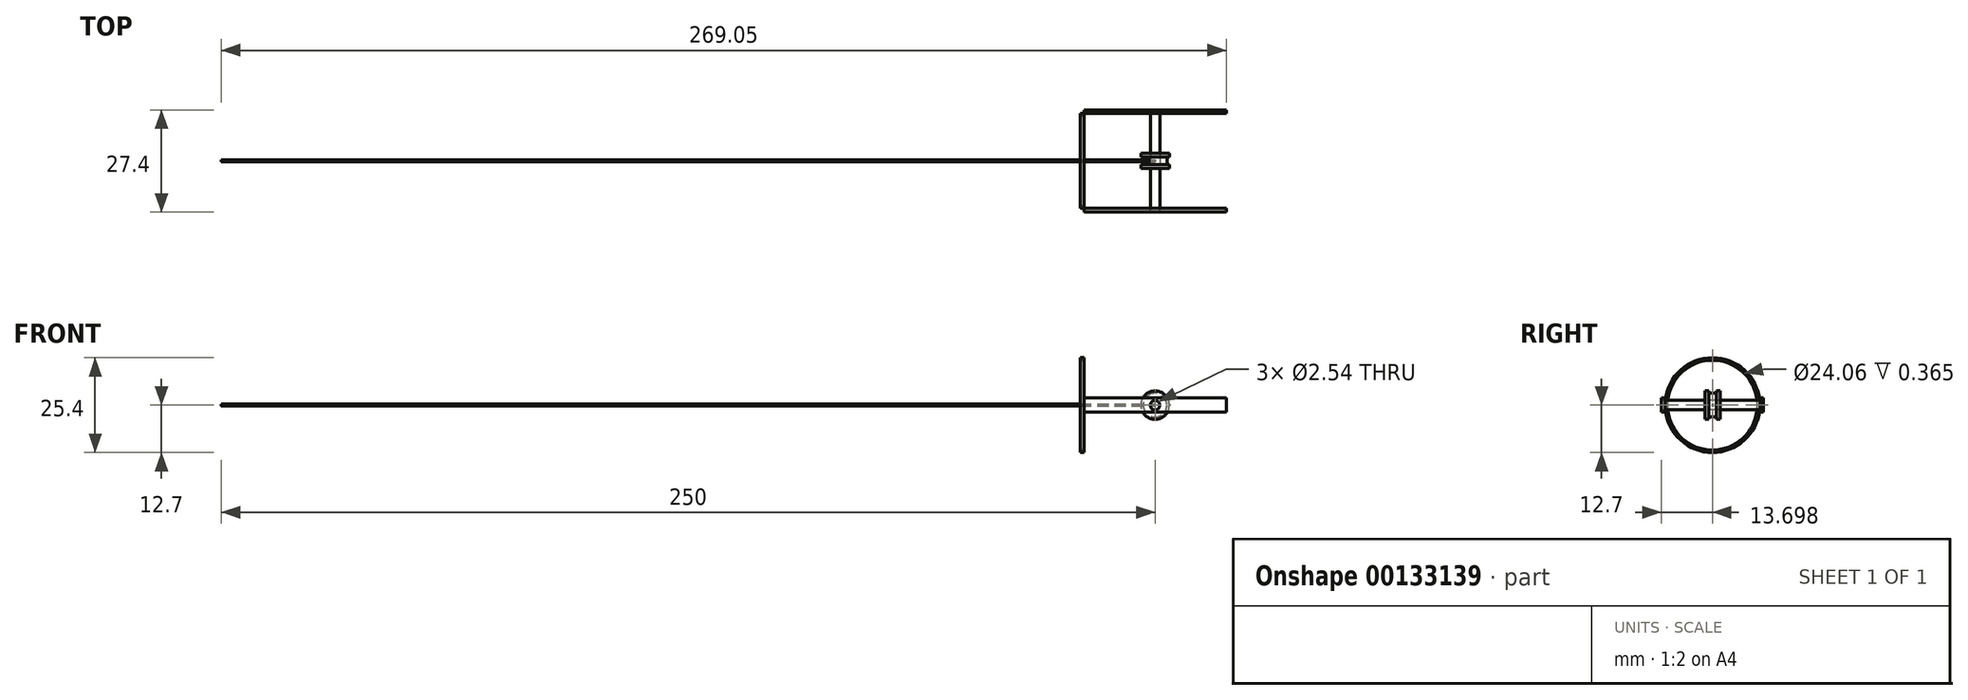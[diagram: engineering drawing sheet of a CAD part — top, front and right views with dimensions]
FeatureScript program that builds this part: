
annotation { "Feature Type Name" : "Feature", "Feature Type Description" : "" }
export const myFeature = defineFeature(function(context is Context, id is Id, definition is map)
    precondition{}
    {
        {
            var Q0;
            Q0=qCreatedBy(makeId("Front.planeOp"),FACE);
            var sketch = newSketch(context, id + "F0", { "sketchPlane" : qUnion([Q0])});
            skCircle(sketch, "E0", {"center": v(0, 0) * mm, "radius": 3.18 * mm});
            skCircle(sketch, "E1", {"center": v(0, 0) * mm, "radius": 3.81 * mm});
            skSolve(sketch);
        }
        {
            var Q0;
            Q0=makeQuery(id+"F0.imprint","IMPRINT",FACE,{"disambiguationData":[TD([[makeQuery(id+"F0.imprint","IMPRINT",EDGE,{"derivedFrom":sQuery(id+"F0.wireOp",EDGE,"E0")}),-1.0]])]});
            var Q1;
            Q1=makeQuery(id+"F0.imprint","IMPRINT",FACE,{"disambiguationData":[TD([[makeQuery(id+"F0.imprint","IMPRINT",EDGE,{"derivedFrom":sQuery(id+"F0.wireOp",EDGE,"E0")}),1.0]])]});
            extrude(context, id + "F1", {"entities" : qUnion([Q0, Q1]), "depth" : 1 * mm});
        }
        {
            var Q0;
            Q0=makeQuery(id+"F1.opExtrude","CAP_FACE",FACE,{"disambiguationData":[OSD([sQuery(id+"F0.wireOp",EDGE,"E1")])],"isStart":false});
            var sketch = newSketch(context, id + "F2", { "sketchPlane" : qUnion([Q0])});
            skCircle(sketch, "E2", {"center": v(0, 0) * mm, "radius": 3.18 * mm});
            skSolve(sketch);
        }
        {
            var Q0;
            Q0=makeQuery(id+"F2.imprint","IMPRINT",FACE,{"disambiguationData":[TD([[makeQuery(id+"F2.imprint","IMPRINT",EDGE,{"derivedFrom":sQuery(id+"F2.wireOp",EDGE,"E2")}),1.0]])]});
            extrude(context, id + "F3", {"entities" : qUnion([Q0]), "operationType" : NewBodyOperationType.ADD, "depth" : 2 * mm});
        }
        {
            var Q0;
            Q0=makeQuery(id+"F3.opExtrude","CAP_FACE",FACE,{"disambiguationData":[OSD([sQuery(id+"F2.wireOp",EDGE,"E2")])],"isStart":false});
            var sketch = newSketch(context, id + "F4", { "sketchPlane" : qUnion([Q0])});
            skCircle(sketch, "E3", {"center": v(0, 0) * mm, "radius": 3.81 * mm});
            skSolve(sketch);
        }
        {
            var Q0;
            Q0=makeQuery(id+"F4.imprint","IMPRINT",FACE,{"disambiguationData":[TD([[makeQuery(id+"F4.imprint","IMPRINT",EDGE,{"derivedFrom":sQuery(id+"F4.wireOp",EDGE,"E3")}),1.0]])]});
            var Q1;
            Q1=makeQuery(id+"F4.imprint","IMPRINT",FACE,{"disambiguationData":[TD([[makeQuery(id+"F4.imprint","IMPRINT",EDGE,{"derivedFrom":makeQuery(id+"F3.opExtrude","CAP_EDGE",EDGE,{"disambiguationData":[OSD([sQuery(id+"F2.wireOp",EDGE,"E2")])],"isStart":false})}),1.0]])]});
            extrude(context, id + "F5", {"entities" : qUnion([Q0, Q1]), "operationType" : NewBodyOperationType.ADD, "depth" : 1 * mm});
        }
        {
            var Q0;
            Q0=makeQuery(id+"F5.opExtrude","CAP_FACE",FACE,{"disambiguationData":[OSD([sQuery(id+"F4.wireOp",EDGE,"E3")])],"isStart":false});
            var sketch = newSketch(context, id + "F6", { "sketchPlane" : qUnion([Q0])});
            skCircle(sketch, "E4", {"center": v(0, 0) * mm, "radius": 1.27 * mm});
            skSolve(sketch);
        }
        {
            var Q0;
            Q0=makeQuery(id+"F6.imprint","IMPRINT",FACE,{"disambiguationData":[TD([[makeQuery(id+"F6.imprint","IMPRINT",EDGE,{"derivedFrom":sQuery(id+"F6.wireOp",EDGE,"E4")}),1.0]])]});
            extrude(context, id + "F7", {"entities" : qUnion([Q0]), "operationType" : NewBodyOperationType.REMOVE, "oppositeDirection" : true, "depth" : 25.4 * mm});
        }
        {
            var Q0;
            Q0=qCreatedBy(makeId("Front.planeOp"),FACE);
            var sketch = newSketch(context, id + "F8", { "sketchPlane" : qUnion([Q0])});
            skCircle(sketch, "E5", {"center": v(0, 0) * mm, "radius": 1.27 * mm});
            skSolve(sketch);
        }
        {
            var Q0;
            Q0=makeQuery(id+"F8.imprint","IMPRINT",FACE,{"disambiguationData":[TD([[makeQuery(id+"F8.imprint","IMPRINT",EDGE,{"derivedFrom":sQuery(id+"F8.wireOp",EDGE,"E5")}),1.0]])]});
            extrude(context, id + "F9", {"entities" : qUnion([Q0]), "oppositeDirection" : true, "depth" : 10.67 * mm});
        }
        {
            var Q0;
            Q0=makeQuery(id+"F9.opExtrude","CAP_FACE",FACE,{"disambiguationData":[OSD([sQuery(id+"F8.wireOp",EDGE,"E5")])],"isStart":true});
            extrude(context, id + "F10", {"entities" : qUnion([Q0]), "depth" : 14.73 * mm});
        }
        {
            var Q0;
            Q0=makeQuery(id+"F9.opExtrude","CAP_FACE",FACE,{"disambiguationData":[OSD([sQuery(id+"F8.wireOp",EDGE,"E5")])],"isStart":false});
            var sketch = newSketch(context, id + "F11", { "sketchPlane" : qUnion([Q0])});
            skLineSegment(sketch, "E6.bottom", {"start": v(19.05, 1.9) * mm, "end": v(-19.05, 1.9) * mm});
            skLineSegment(sketch, "E6.top", {"start": v(19.05, -1.9) * mm, "end": v(-19.05, -1.9) * mm});
            skLineSegment(sketch, "E6.left", {"start": v(19.05, 1.9) * mm, "end": v(19.05, -1.9) * mm});
            skLineSegment(sketch, "E6.right", {"start": v(-19.05, 1.9) * mm, "end": v(-19.05, -1.9) * mm});
            skPoint(sketch, "E6.middle", {"position": v(0, 0) * mm});
            skSolve(sketch);
        }
        {
            var Q0;
            Q0=makeQuery(id+"F11.imprint","IMPRINT",FACE,{"disambiguationData":[TD([[makeQuery(id+"F11.imprint","IMPRINT",EDGE,{"derivedFrom":sQuery(id+"F11.wireOp",EDGE,"E6.bottom")}),1.0]])]});
            extrude(context, id + "F12", {"entities" : qUnion([Q0]), "depth" : 1 * mm});
        }
        {
            var Q0;
            Q0=makeQuery(id+"F10.opExtrude","CAP_FACE",FACE,{"disambiguationData":[OSD([sQuery(id+"F8.wireOp",EDGE,"E5")])],"isStart":false});
            var sketch = newSketch(context, id + "F13", { "sketchPlane" : qUnion([Q0])});
            skLineSegment(sketch, "E7.bottom", {"start": v(19.05, 1.9) * mm, "end": v(-19.05, 1.9) * mm});
            skLineSegment(sketch, "E7.top", {"start": v(19.05, -1.9) * mm, "end": v(-19.05, -1.9) * mm});
            skLineSegment(sketch, "E7.left", {"start": v(19.05, 1.9) * mm, "end": v(19.05, -1.9) * mm});
            skLineSegment(sketch, "E7.right", {"start": v(-19.05, 1.9) * mm, "end": v(-19.05, -1.9) * mm});
            skPoint(sketch, "E7.middle", {"position": v(0, 0) * mm});
            skSolve(sketch);
        }
        {
            var Q0;
            Q0=makeQuery(id+"F13.imprint","IMPRINT",FACE,{"disambiguationData":[TD([[makeQuery(id+"F13.imprint","IMPRINT",EDGE,{"derivedFrom":sQuery(id+"F13.wireOp",EDGE,"E7.bottom")}),1.0]])]});
            extrude(context, id + "F14", {"entities" : qUnion([Q0]), "depth" : 1 * mm});
        }
        {
            var Q0;
            Q0=makeQuery(id+"F14.opExtrude","SWEPT_FACE",FACE,{"disambiguationData":[OSD([sQuery(id+"F13.wireOp",EDGE,"E7.right")])]});
            var sketch = newSketch(context, id + "F15", { "sketchPlane" : qUnion([Q0])});
            skCircle(sketch, "E8", {"center": v(2.03, 0) * mm, "radius": 12.7 * mm});
            skCircle(sketch, "E9", {"center": v(2.03, 0) * mm, "radius": 12.03 * mm});
            skSolve(sketch);
        }
        {
            var Q0;
            Q0=makeQuery(id+"F15.imprint","IMPRINT",FACE,{"disambiguationData":[TD([[makeQuery(id+"F15.imprint","IMPRINT",EDGE,{"derivedFrom":sQuery(id+"F15.wireOp",EDGE,"E8")}),1.0]])]});
            extrude(context, id + "F16", {"entities" : qUnion([Q0]), "depth" : 1 * mm});
        }
        {
            var Q0;
            Q0=makeQuery(id+"F16.opExtrude","CAP_EDGE",EDGE,{"disambiguationData":[OSD([sQuery(id+"F15.wireOp",EDGE,"E9")])],"isStart":false});
            fillet(context, id + "F17", {"entities" : qUnion([Q0]), "radius" : 0.64 * mm, "tangentPropagation" : true, "allowEdgeOverflow" : false});
        }
        {
            var Q0;
            Q0=qCreatedBy(makeId("Right.planeOp"),FACE);
            var sketch = newSketch(context, id + "F18", { "sketchPlane" : qUnion([Q0])});
            skCircle(sketch, "E10", {"center": v(-1.93, 0) * mm, "radius": 0.25 * mm});
            skSolve(sketch);
        }
        {
            var Q0;
            Q0 = qSketchRegion(id + "F18", true);
            extrude(context, id + "F19", {"entities" : qUnion([Q0]), "oppositeDirection" : true, "depth" : 250 * mm});
        }
    });
